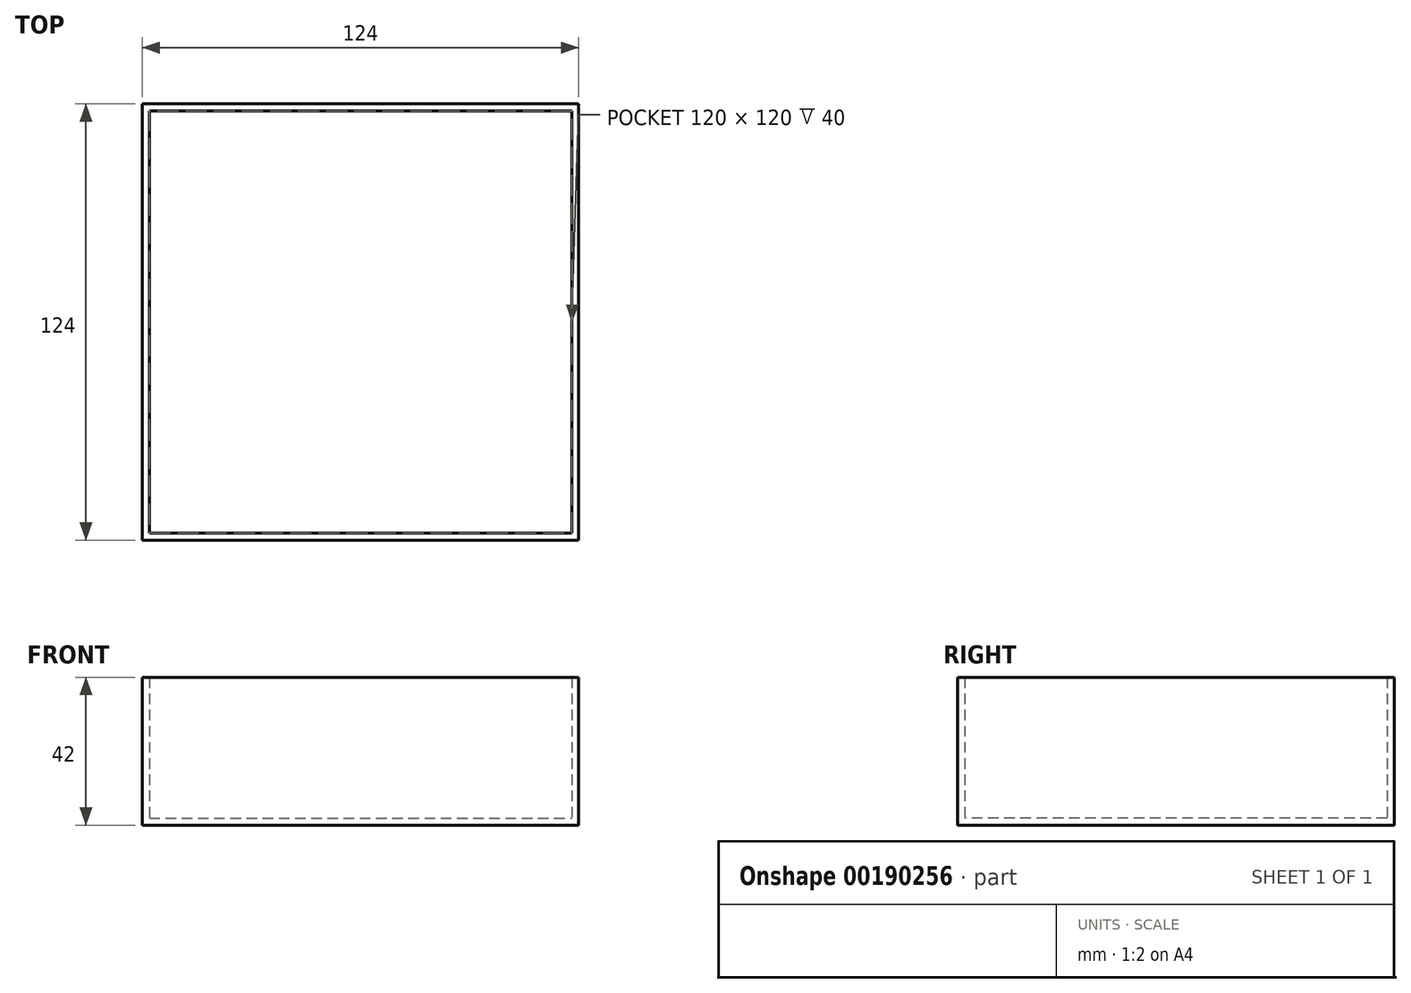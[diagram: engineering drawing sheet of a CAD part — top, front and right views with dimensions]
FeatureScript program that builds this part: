
annotation { "Feature Type Name" : "Feature", "Feature Type Description" : "" }
export const myFeature = defineFeature(function(context is Context, id is Id, definition is map)
    precondition{}
    {
        {
            var Q0;
            Q0=qCreatedBy(makeId("Top.planeOp"),FACE);
            var sketch = newSketch(context, id + "F0", { "sketchPlane" : qUnion([Q0])});
            skLineSegment(sketch, "E0.bottom", {"start": v(-60, 60) * mm, "end": v(60, 60) * mm});
            skLineSegment(sketch, "E0.top", {"start": v(-60, -60) * mm, "end": v(60, -60) * mm});
            skLineSegment(sketch, "E0.left", {"start": v(-60, 60) * mm, "end": v(-60, -60) * mm});
            skLineSegment(sketch, "E0.right", {"start": v(60, 60) * mm, "end": v(60, -60) * mm});
            skPoint(sketch, "E0.middle", {"position": v(0, 0) * mm});
            skLineSegment(sketch, "E1.bottom", {"start": v(-62, 62) * mm, "end": v(62, 62) * mm});
            skLineSegment(sketch, "E1.top", {"start": v(-62, -62) * mm, "end": v(62, -62) * mm});
            skLineSegment(sketch, "E1.left", {"start": v(-62, 62) * mm, "end": v(-62, -62) * mm});
            skLineSegment(sketch, "E1.right", {"start": v(62, 62) * mm, "end": v(62, -62) * mm});
            skSolve(sketch);
        }
        {
            var Q0;
            Q0=makeQuery(id+"F0.imprint","IMPRINT",FACE,{"disambiguationData":[TD([[makeQuery(id+"F0.imprint","IMPRINT",EDGE,{"derivedFrom":sQuery(id+"F0.wireOp",EDGE,"E0.bottom")}),1.0]])]});
            var Q1;
            Q1=makeQuery(id+"F0.imprint","IMPRINT",FACE,{"disambiguationData":[TD([[makeQuery(id+"F0.imprint","IMPRINT",EDGE,{"derivedFrom":sQuery(id+"F0.wireOp",EDGE,"E0.bottom")}),-1.0]])]});
            extrude(context, id + "F1", {"entities" : qUnion([Q0, Q1]), "oppositeDirection" : true, "depth" : 2 * mm});
        }
        {
            var Q0;
            Q0=makeQuery(id+"F0.imprint","IMPRINT",FACE,{"disambiguationData":[TD([[makeQuery(id+"F0.imprint","IMPRINT",EDGE,{"derivedFrom":sQuery(id+"F0.wireOp",EDGE,"E0.bottom")}),1.0]])]});
            extrude(context, id + "F2", {"entities" : qUnion([Q0]), "operationType" : NewBodyOperationType.ADD, "depth" : 40 * mm});
        }
    });
